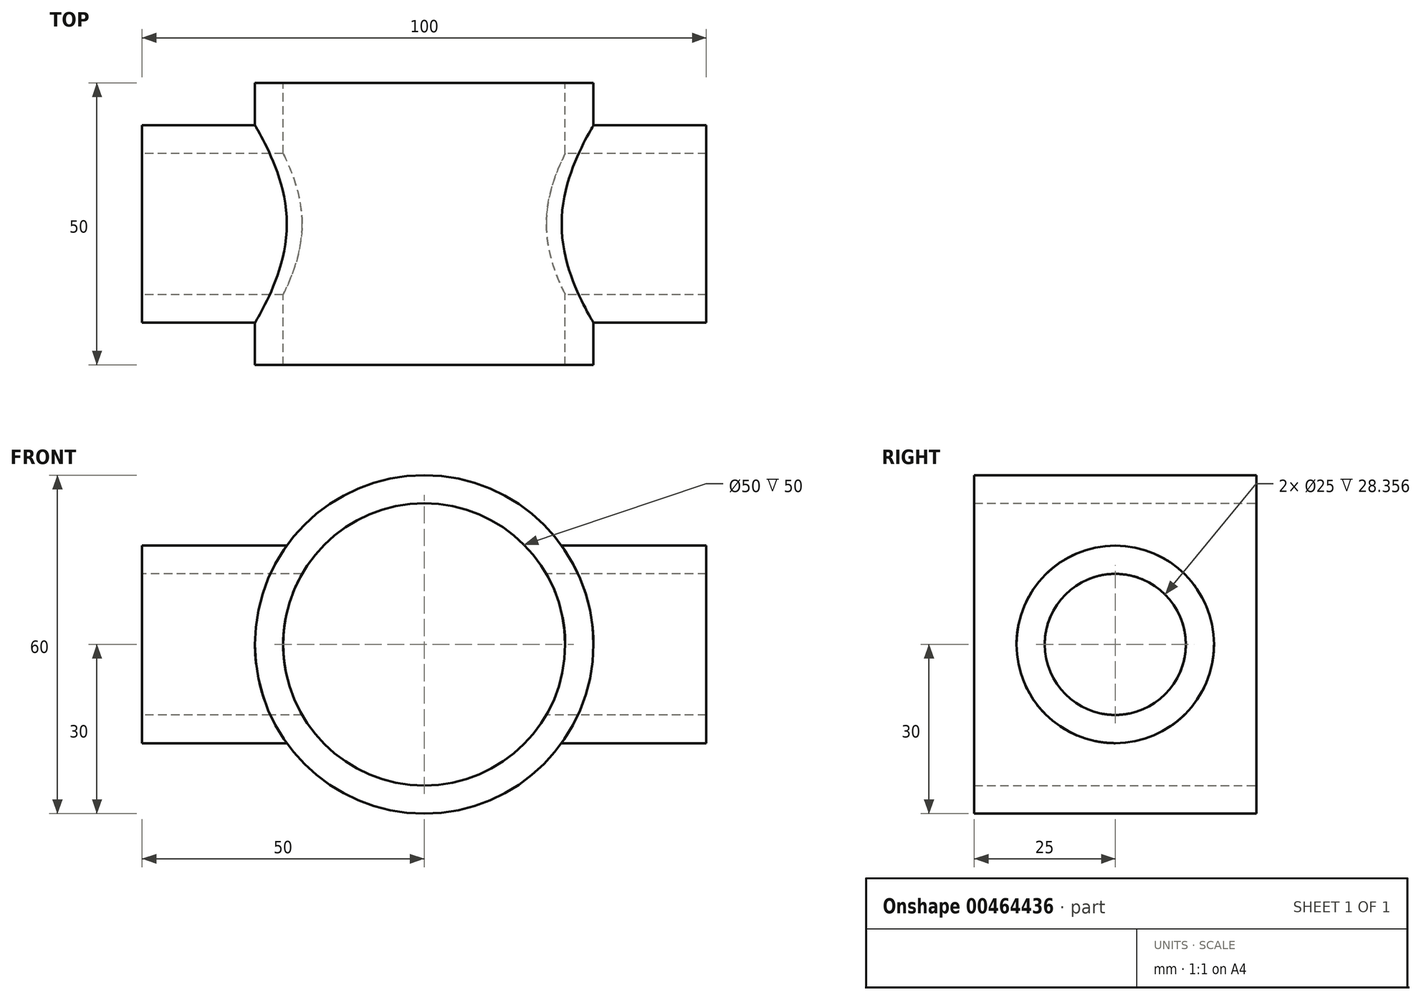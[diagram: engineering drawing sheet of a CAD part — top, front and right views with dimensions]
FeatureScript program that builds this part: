
annotation { "Feature Type Name" : "Feature", "Feature Type Description" : "" }
export const myFeature = defineFeature(function(context is Context, id is Id, definition is map)
    precondition{}
    {
        {
            var Q0;
            Q0=qCreatedBy(makeId("Front.planeOp"),FACE);
            var sketch = newSketch(context, id + "F0", { "sketchPlane" : qUnion([Q0])});
            skCircle(sketch, "E0", {"center": v(0, 0) * mm, "radius": 25 * mm});
            skCircle(sketch, "E1.0", {"center": v(0, 0) * mm, "radius": 30 * mm});
            skSolve(sketch);
        }
        {
            var Q0;
            Q0=qSketchRegion(id+"F0",true);
            extrude(context, id + "F1", {"entities" : qUnion([Q0]), "depth" : 25 * mm, "hasSecondDirection" : true, "secondDirectionOppositeDirection" : true, "secondDirectionDepth" : 25 * mm});
        }
        {
            var Q0;
            Q0=qCreatedBy(makeId("Right.planeOp"),FACE);
            var sketch = newSketch(context, id + "F2", { "sketchPlane" : qUnion([Q0])});
            skCircle(sketch, "E2", {"center": v(0, 0) * mm, "radius": 12.5 * mm});
            skCircle(sketch, "E3.0", {"center": v(0, 0) * mm, "radius": 17.5 * mm});
            skSolve(sketch);
        }
        {
            var Q0;
            Q0=qSketchRegion(id+"F2",true);
            extrude(context, id + "F3", {"entities" : qUnion([Q0]), "operationType" : NewBodyOperationType.ADD, "depth" : 50 * mm, "hasSecondDirection" : true, "secondDirectionOppositeDirection" : true, "secondDirectionDepth" : 50 * mm});
        }
        {
            var Q0;
            Q0=makeQuery(id+"F1.opExtrude","CAP_FACE",FACE,{"disambiguationData":[OSD([sQuery(id+"F0.wireOp",EDGE,"E0"),sQuery(id+"F0.wireOp",EDGE,"E1.0")])],"isStart":false});
            var sketch = newSketch(context, id + "F4", { "sketchPlane" : qUnion([Q0])});
            skCircle(sketch, "E4", {"center": v(0, 0) * mm, "radius": 25 * mm});
            skSolve(sketch);
        }
        {
            var Q0;
            Q0=qSketchRegion(id+"F4",true);
            var Q1;
            Q1=makeQuery(id+"F1.opExtrude","CAP_FACE",FACE,{"disambiguationData":[OSD([sQuery(id+"F0.wireOp",EDGE,"E0"),sQuery(id+"F0.wireOp",EDGE,"E1.0")])],"isStart":true});
            extrude(context, id + "F5", {"entities" : qUnion([Q0]), "operationType" : NewBodyOperationType.REMOVE, "endBound" : BoundingType.UP_TO_SURFACE, "oppositeDirection" : true, "endBoundEntityFace" : qUnion([Q1]), "depth" : 25 * mm});
        }
        {
            var Q0;
            Q0=makeQuery(id+"F3.opExtrude","CAP_FACE",FACE,{"disambiguationData":[OSD([sQuery(id+"F2.wireOp",EDGE,"E2"),sQuery(id+"F2.wireOp",EDGE,"E3.0")])],"isStart":false});
            var sketch = newSketch(context, id + "F6", { "sketchPlane" : qUnion([Q0])});
            skCircle(sketch, "E5", {"center": v(0, 0) * mm, "radius": 12.5 * mm});
            skSolve(sketch);
        }
        {
            var Q0;
            Q0=qSketchRegion(id+"F6",true);
            extrude(context, id + "F7", {"entities" : qUnion([Q0]), "operationType" : NewBodyOperationType.REMOVE, "endBound" : BoundingType.THROUGH_ALL, "oppositeDirection" : true, "depth" : 25 * mm});
        }
    });
